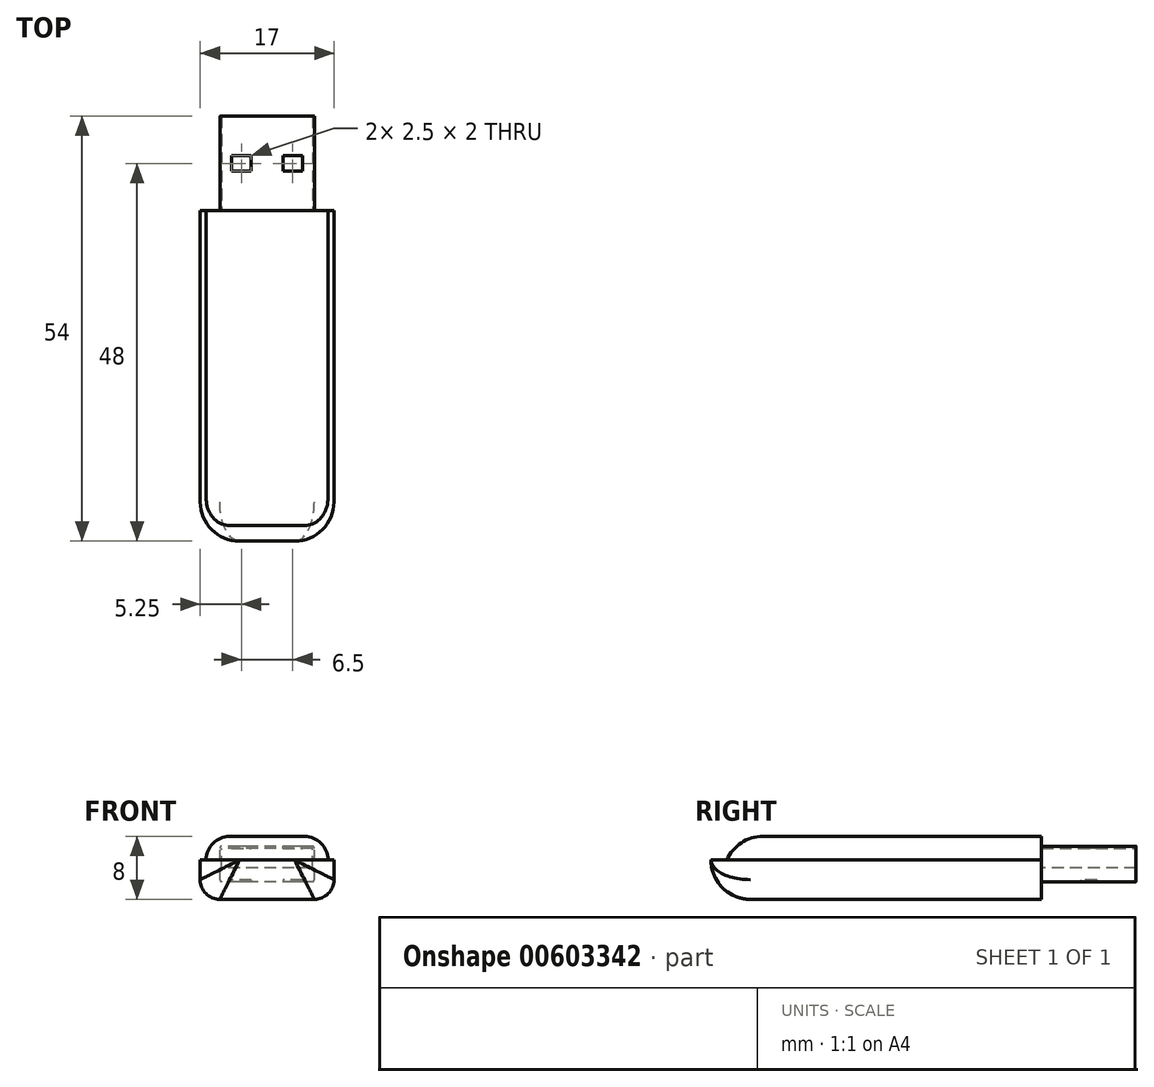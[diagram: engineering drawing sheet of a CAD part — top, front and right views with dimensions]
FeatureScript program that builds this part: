
annotation { "Feature Type Name" : "Feature", "Feature Type Description" : "" }
export const myFeature = defineFeature(function(context is Context, id is Id, definition is map)
    precondition{}
    {
        {
            var Q0;
            Q0=qCreatedBy(makeId("Front.planeOp"),FACE);
            var sketch = newSketch(context, id + "F0", { "sketchPlane" : qUnion([Q0])});
            skLineSegment(sketch, "E0", {"start": v(0, 5) * mm, "end": v(0, 0) * mm});
            skLineSegment(sketch, "E1", {"start": v(0, 0) * mm, "end": v(17, 0) * mm});
            skLineSegment(sketch, "E2", {"start": v(17, 0) * mm, "end": v(17, 5) * mm});
            skLineSegment(sketch, "E3", {"start": v(0, 5) * mm, "end": v(17, 5) * mm});
            skSolve(sketch);
        }
        {
            var Q0;
            Q0=makeQuery(id+"F0.imprint","IMPRINT",FACE,{"disambiguationData":[TD([[makeQuery(id+"F0.imprint","IMPRINT",EDGE,{"derivedFrom":sQuery(id+"F0.wireOp",EDGE,"E0")}),1.0]])]});
            extrude(context, id + "F1", {"entities" : qUnion([Q0]), "depth" : 42 * mm, "offsetDistance" : 25 * mm});
        }
        {
            var Q0;
            Q0=makeQuery(id+"F1.opExtrude","SWEPT_BODY",BODY,{"disambiguationData":[OSD([sQuery(id+"F0.wireOp",EDGE,"E0"),sQuery(id+"F0.wireOp",EDGE,"E1"),sQuery(id+"F0.wireOp",EDGE,"E2"),sQuery(id+"F0.wireOp",EDGE,"E3")])]});
            transform(context, id + "F2", {"entities" : qUnion([Q0]), "transformType" : TransformType.TRANSLATION_3D, "dx" : -8.5 * mm, "dy" : 0 * mm, "dz" : -4 * mm, "makeCopy" : false});
        }
        {
            var Q0;
            Q0=makeQuery(id+"F1.opExtrude","SWEPT_EDGE",EDGE,{"disambiguationData":[OSD([sQuery(id+"F0.wireOp",EDGE,"E1"),sQuery(id+"F0.wireOp",EDGE,"E2")])]});
            var Q1;
            Q1=makeQuery(id+"F1.opExtrude","SWEPT_EDGE",EDGE,{"disambiguationData":[OSD([sQuery(id+"F0.wireOp",EDGE,"E0"),sQuery(id+"F0.wireOp",EDGE,"E1")])]});
            fillet(context, id + "F3", {"entities" : qUnion([Q0, Q1]), "radius" : 2.5 * mm, "tangentPropagation" : true, "allowEdgeOverflow" : false});
        }
        {
            var Q0;
            Q0=makeQuery(id+"F1.opExtrude","CAP_FACE",FACE,{"disambiguationData":[OSD([sQuery(id+"F0.wireOp",EDGE,"E0"),sQuery(id+"F0.wireOp",EDGE,"E1"),sQuery(id+"F0.wireOp",EDGE,"E2"),sQuery(id+"F0.wireOp",EDGE,"E3")])],"isStart":true});
            var sketch = newSketch(context, id + "F4", { "sketchPlane" : qUnion([Q0])});
            skLineSegment(sketch, "E4.bottom", {"start": v(-7.75, 1) * mm, "end": v(7.75, 1) * mm});
            skLineSegment(sketch, "E4.top", {"start": v(-7.75, 4) * mm, "end": v(7.75, 4) * mm});
            skLineSegment(sketch, "E4.left", {"start": v(-7.75, 1) * mm, "end": v(-7.75, 4) * mm});
            skLineSegment(sketch, "E4.right", {"start": v(7.75, 1) * mm, "end": v(7.75, 4) * mm});
            skSolve(sketch);
        }
        {
            var Q0;
            Q0=makeQuery(id+"F4.imprint","IMPRINT",FACE,{"disambiguationData":[TD([[makeQuery(id+"F4.imprint","IMPRINT",EDGE,{"derivedFrom":sQuery(id+"F4.wireOp",EDGE,"E4.bottom")}),-1.0]])]});
            extrude(context, id + "F5", {"entities" : qUnion([Q0]), "operationType" : NewBodyOperationType.ADD, "oppositeDirection" : true, "depth" : 40 * mm, "offsetDistance" : 25 * mm});
        }
        {
            var Q0;
            Q0=makeQuery(id+"F5.opExtrude","CAP_EDGE",EDGE,{"disambiguationData":[OSD([sQuery(id+"F4.wireOp",EDGE,"E4.top")])],"isStart":false});
            fillet(context, id + "F6", {"entities" : qUnion([Q0]), "radius" : 5 * mm, "tangentPropagation" : true, "allowEdgeOverflow" : false});
        }
        {
            var Q0;
            Q0=makeQuery(id+"F5.opExtrude","SWEPT_EDGE",EDGE,{"disambiguationData":[OSD([sQuery(id+"F4.wireOp",EDGE,"E4.top"),sQuery(id+"F4.wireOp",EDGE,"E4.left")])]});
            var Q1;
            Q1=makeQuery(id+"F5.opExtrude","SWEPT_EDGE",EDGE,{"disambiguationData":[OSD([sQuery(id+"F4.wireOp",EDGE,"E4.top"),sQuery(id+"F4.wireOp",EDGE,"E4.right")])]});
            fillet(context, id + "F7", {"entities" : qUnion([Q0, Q1]), "radius" : 3 * mm, "tangentPropagation" : true, "allowEdgeOverflow" : false});
        }
        {
            var Q0;
            Q0=makeQuery(id+"F1.opExtrude","CAP_EDGE",EDGE,{"disambiguationData":[OSD([sQuery(id+"F0.wireOp",EDGE,"E1")])],"isStart":false});
            fillet(context, id + "F8", {"entities" : qUnion([Q0]), "radius" : 5 * mm, "tangentPropagation" : true, "allowEdgeOverflow" : false});
        }
        {
            var Q0;
            Q0=makeQuery(id+"F5.boolean.opBoolean","MERGE",FACE,{"derivedFrom":[makeQuery(id+"F1.opExtrude","CAP_FACE",FACE,{"disambiguationData":[OSD([sQuery(id+"F0.wireOp",EDGE,"E0"),sQuery(id+"F0.wireOp",EDGE,"E1"),sQuery(id+"F0.wireOp",EDGE,"E2"),sQuery(id+"F0.wireOp",EDGE,"E3")])],"isStart":true}),makeQuery(id+"F5.opExtrude","CAP_FACE",FACE,{"disambiguationData":[OSD([sQuery(id+"F4.wireOp",EDGE,"E4.bottom"),sQuery(id+"F4.wireOp",EDGE,"E4.top"),sQuery(id+"F4.wireOp",EDGE,"E4.left"),sQuery(id+"F4.wireOp",EDGE,"E4.right")])],"isStart":true})]});
            var sketch = newSketch(context, id + "F9", { "sketchPlane" : qUnion([Q0])});
            skLineSegment(sketch, "E5.bottom", {"start": v(-6, -1.75) * mm, "end": v(6, -1.75) * mm});
            skLineSegment(sketch, "E5.top", {"start": v(-6, 2.75) * mm, "end": v(6, 2.75) * mm});
            skLineSegment(sketch, "E5.left", {"start": v(-6, -1.75) * mm, "end": v(-6, 2.75) * mm});
            skLineSegment(sketch, "E5.right", {"start": v(6, -1.75) * mm, "end": v(6, 2.75) * mm});
            skSolve(sketch);
        }
        {
            var Q0;
            Q0=makeQuery(id+"F9.imprint","IMPRINT",FACE,{"disambiguationData":[TD([[makeQuery(id+"F9.imprint","IMPRINT",EDGE,{"derivedFrom":sQuery(id+"F9.wireOp",EDGE,"E5.bottom")}),1.0]])]});
            extrude(context, id + "F10", {"entities" : qUnion([Q0]), "operationType" : NewBodyOperationType.ADD, "depth" : 12 * mm, "offsetDistance" : 25 * mm});
        }
        {
            var Q0;
            Q0=makeQuery(id+"F10.opExtrude","CAP_FACE",FACE,{"disambiguationData":[OSD([sQuery(id+"F9.wireOp",EDGE,"E5.bottom"),sQuery(id+"F9.wireOp",EDGE,"E5.top"),sQuery(id+"F9.wireOp",EDGE,"E5.left"),sQuery(id+"F9.wireOp",EDGE,"E5.right")])],"isStart":false});
            var sketch = newSketch(context, id + "F11", { "sketchPlane" : qUnion([Q0])});
            skLineSegment(sketch, "E6.bottom", {"start": v(-5.75, -1.5) * mm, "end": v(5.75, -1.5) * mm});
            skLineSegment(sketch, "E6.top", {"start": v(-5.75, 2.5) * mm, "end": v(5.75, 2.5) * mm});
            skLineSegment(sketch, "E6.left", {"start": v(-5.75, -1.5) * mm, "end": v(-5.75, 2.5) * mm});
            skLineSegment(sketch, "E6.right", {"start": v(5.75, -1.5) * mm, "end": v(5.75, 2.5) * mm});
            skSolve(sketch);
        }
        {
            var Q0;
            Q0=makeQuery(id+"F11.imprint","IMPRINT",FACE,{"disambiguationData":[TD([[makeQuery(id+"F11.imprint","IMPRINT",EDGE,{"derivedFrom":sQuery(id+"F11.wireOp",EDGE,"E6.bottom")}),1.0]])]});
            extrude(context, id + "F12", {"entities" : qUnion([Q0]), "operationType" : NewBodyOperationType.REMOVE, "oppositeDirection" : true, "depth" : 12 * mm, "offsetDistance" : 25 * mm});
        }
        {
            var Q0;
            Q0=makeQuery(id+"F10.opExtrude","SWEPT_FACE",FACE,{"disambiguationData":[OSD([sQuery(id+"F9.wireOp",EDGE,"E5.top")])]});
            var sketch = newSketch(context, id + "F13", { "sketchPlane" : qUnion([Q0])});
            skLineSegment(sketch, "E7.bottom", {"start": v(4.5, 5) * mm, "end": v(2, 5) * mm});
            skLineSegment(sketch, "E7.top", {"start": v(4.5, 7) * mm, "end": v(2, 7) * mm});
            skLineSegment(sketch, "E7.left", {"start": v(4.5, 5) * mm, "end": v(4.5, 7) * mm});
            skLineSegment(sketch, "E7.right", {"start": v(2, 5) * mm, "end": v(2, 7) * mm});
            skSolve(sketch);
        }
        {
            var Q0;
            Q0=makeQuery(id+"F13.imprint","IMPRINT",FACE,{"disambiguationData":[TD([[makeQuery(id+"F13.imprint","IMPRINT",EDGE,{"derivedFrom":sQuery(id+"F13.wireOp",EDGE,"E7.bottom")}),-1.0]])]});
            extrude(context, id + "F14", {"entities" : qUnion([Q0]), "operationType" : NewBodyOperationType.REMOVE, "oppositeDirection" : true, "depth" : 2.5 * mm, "offsetDistance" : 25 * mm});
        }
        {
            var Q0;
            Q0=makeQuery(id+"F10.opExtrude","SWEPT_FACE",FACE,{"disambiguationData":[OSD([sQuery(id+"F9.wireOp",EDGE,"E5.top")])]});
            var sketch = newSketch(context, id + "F15", { "sketchPlane" : qUnion([Q0])});
            skLineSegment(sketch, "E8.bottom", {"start": v(-2, 5) * mm, "end": v(-4.5, 5) * mm});
            skLineSegment(sketch, "E8.top", {"start": v(-2, 7) * mm, "end": v(-4.5, 7) * mm});
            skLineSegment(sketch, "E8.left", {"start": v(-2, 5) * mm, "end": v(-2, 7) * mm});
            skLineSegment(sketch, "E8.right", {"start": v(-4.5, 5) * mm, "end": v(-4.5, 7) * mm});
            skSolve(sketch);
        }
        {
            var Q0;
            Q0 = qSketchRegion(id + "F15", true);
            extrude(context, id + "F16", {"entities" : qUnion([Q0]), "operationType" : NewBodyOperationType.REMOVE, "oppositeDirection" : true, "depth" : 2.5 * mm, "offsetDistance" : 25 * mm});
        }
        {
            var Q0;
            Q0=makeQuery(id+"F10.opExtrude","SWEPT_FACE",FACE,{"disambiguationData":[OSD([sQuery(id+"F9.wireOp",EDGE,"E5.bottom")])]});
            var sketch = newSketch(context, id + "F17", { "sketchPlane" : qUnion([Q0])});
            skLineSegment(sketch, "E9.bottom", {"start": v(4.5, -7) * mm, "end": v(2, -7) * mm});
            skLineSegment(sketch, "E9.top", {"start": v(4.5, -5) * mm, "end": v(2, -5) * mm});
            skLineSegment(sketch, "E9.left", {"start": v(4.5, -7) * mm, "end": v(4.5, -5) * mm});
            skLineSegment(sketch, "E9.right", {"start": v(2, -7) * mm, "end": v(2, -5) * mm});
            skSolve(sketch);
        }
        {
            var Q0;
            Q0=makeQuery(id+"F17.imprint","IMPRINT",FACE,{"disambiguationData":[TD([[makeQuery(id+"F17.imprint","IMPRINT",EDGE,{"derivedFrom":sQuery(id+"F17.wireOp",EDGE,"E9.bottom")}),-1.0]])]});
            extrude(context, id + "F18", {"entities" : qUnion([Q0]), "operationType" : NewBodyOperationType.REMOVE, "oppositeDirection" : true, "depth" : 2.5 * mm, "offsetDistance" : 25 * mm});
        }
        {
            var Q0;
            Q0=makeQuery(id+"F10.opExtrude","SWEPT_FACE",FACE,{"disambiguationData":[OSD([sQuery(id+"F9.wireOp",EDGE,"E5.bottom")])]});
            var sketch = newSketch(context, id + "F19", { "sketchPlane" : qUnion([Q0])});
            skLineSegment(sketch, "E10.bottom", {"start": v(-2, -7) * mm, "end": v(-4.5, -7) * mm});
            skLineSegment(sketch, "E10.top", {"start": v(-2, -5) * mm, "end": v(-4.5, -5) * mm});
            skLineSegment(sketch, "E10.left", {"start": v(-2, -7) * mm, "end": v(-2, -5) * mm});
            skLineSegment(sketch, "E10.right", {"start": v(-4.5, -7) * mm, "end": v(-4.5, -5) * mm});
            skSolve(sketch);
        }
        {
            var Q0;
            Q0=makeQuery(id+"F19.imprint","IMPRINT",FACE,{"disambiguationData":[TD([[makeQuery(id+"F19.imprint","IMPRINT",EDGE,{"derivedFrom":sQuery(id+"F19.wireOp",EDGE,"E10.bottom")}),-1.0]])]});
            extrude(context, id + "F20", {"entities" : qUnion([Q0]), "operationType" : NewBodyOperationType.REMOVE, "oppositeDirection" : true, "depth" : 2.5 * mm, "offsetDistance" : 25 * mm});
        }
        {
            var Q0;
            Q0=makeQuery(id+"F12.boolean.opBoolean","COPY",FACE,{"derivedFrom":makeQuery(id+"F12.opExtrude","CAP_FACE",FACE,{"disambiguationData":[OSD([sQuery(id+"F11.wireOp",EDGE,"E6.bottom"),sQuery(id+"F11.wireOp",EDGE,"E6.top"),sQuery(id+"F11.wireOp",EDGE,"E6.left"),sQuery(id+"F11.wireOp",EDGE,"E6.right")])],"isStart":false})});
            var sketch = newSketch(context, id + "F21", { "sketchPlane" : qUnion([Q0])});
            skLineSegment(sketch, "E11.bottom", {"start": v(-5.75, -1.5) * mm, "end": v(5.75, -1.5) * mm});
            skLineSegment(sketch, "E11.top", {"start": v(-5.75, 0) * mm, "end": v(5.75, 0) * mm});
            skLineSegment(sketch, "E11.left", {"start": v(-5.75, -1.5) * mm, "end": v(-5.75, 0) * mm});
            skLineSegment(sketch, "E11.right", {"start": v(5.75, -1.5) * mm, "end": v(5.75, 0) * mm});
            skSolve(sketch);
        }
        {
            var Q0;
            Q0=makeQuery(id+"F21.imprint","IMPRINT",FACE,{"disambiguationData":[TD([[makeQuery(id+"F21.imprint","IMPRINT",EDGE,{"derivedFrom":sQuery(id+"F21.wireOp",EDGE,"E11.bottom")}),1.0]])]});
            extrude(context, id + "F22", {"entities" : qUnion([Q0]), "operationType" : NewBodyOperationType.ADD, "depth" : 12 * mm, "offsetDistance" : 25 * mm});
        }
        {
            var Q0;
            Q0=makeQuery(id+"F10.opExtrude","SWEPT_EDGE",EDGE,{"disambiguationData":[OSD([sQuery(id+"F9.wireOp",EDGE,"E5.top"),sQuery(id+"F9.wireOp",EDGE,"E5.right")])]});
            var Q1;
            Q1=makeQuery(id+"F10.opExtrude","SWEPT_EDGE",EDGE,{"disambiguationData":[OSD([sQuery(id+"F9.wireOp",EDGE,"E5.bottom"),sQuery(id+"F9.wireOp",EDGE,"E5.right")])]});
            var Q2;
            Q2=makeQuery(id+"F10.opExtrude","SWEPT_EDGE",EDGE,{"disambiguationData":[OSD([sQuery(id+"F9.wireOp",EDGE,"E5.bottom"),sQuery(id+"F9.wireOp",EDGE,"E5.left")])]});
            var Q3;
            Q3=makeQuery(id+"F10.opExtrude","SWEPT_EDGE",EDGE,{"disambiguationData":[OSD([sQuery(id+"F9.wireOp",EDGE,"E5.top"),sQuery(id+"F9.wireOp",EDGE,"E5.left")])]});
            fillet(context, id + "F23", {"entities" : qUnion([Q0, Q1, Q2, Q3]), "radius" : 0.25 * mm, "tangentPropagation" : true, "allowEdgeOverflow" : false});
        }
    });
